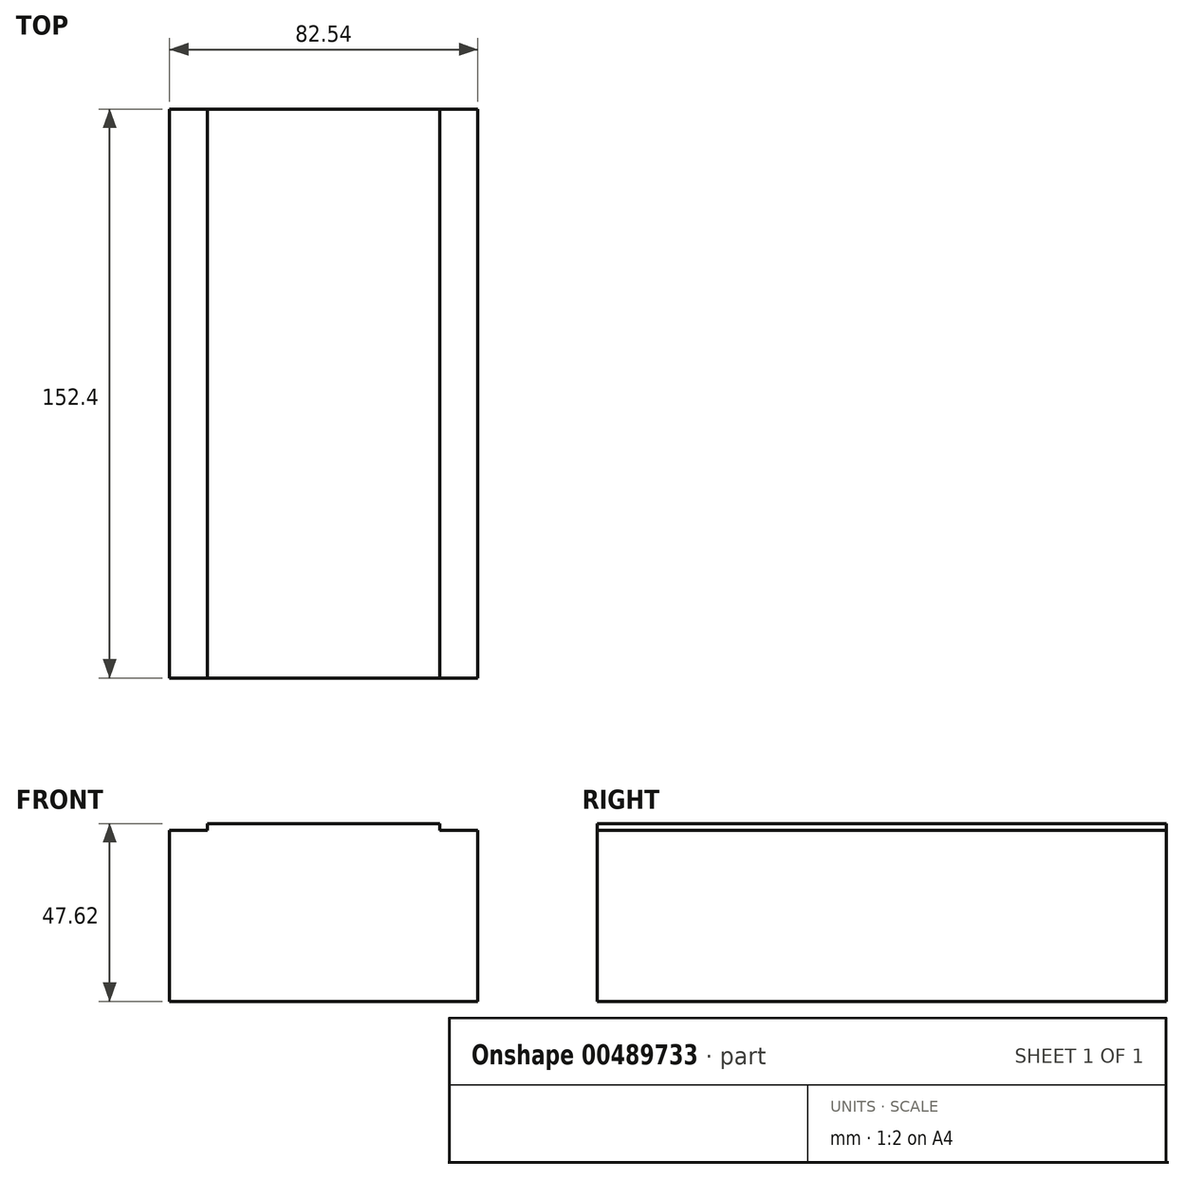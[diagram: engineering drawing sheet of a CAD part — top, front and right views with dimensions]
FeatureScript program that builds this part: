
annotation { "Feature Type Name" : "Feature", "Feature Type Description" : "" }
export const myFeature = defineFeature(function(context is Context, id is Id, definition is map)
    precondition{}
    {
        {
            var Q0;
            Q0=qCreatedBy(makeId("Front.planeOp"),FACE);
            var sketch = newSketch(context, id + "F0", { "sketchPlane" : qUnion([Q0])});
            skLineSegment(sketch, "E0.bottom", {"start": v(31.11, 23.81) * mm, "end": v(-31.11, 23.81) * mm});
            skLineSegment(sketch, "E0.top", {"start": v(41.27, -23.81) * mm, "end": v(-41.28, -23.81) * mm});
            skLineSegment(sketch, "E0.left", {"start": v(41.28, 22.03) * mm, "end": v(41.27, -23.81) * mm});
            skLineSegment(sketch, "E0.right", {"start": v(-41.27, 22.03) * mm, "end": v(-41.28, -23.81) * mm});
            skPoint(sketch, "E0.middle", {"position": v(0, 0) * mm});
            skLineSegment(sketch, "E1.top", {"start": v(-41.27, 22.03) * mm, "end": v(-31.11, 22.03) * mm});
            skLineSegment(sketch, "E1.right", {"start": v(-31.11, 23.81) * mm, "end": v(-31.11, 22.03) * mm});
            skPoint(sketch, "E2.orphan", {"position": v(-41.27, 23.81) * mm});
            skLineSegment(sketch, "E3.MirrorCS", {"start": v(41.27, 22.03) * mm, "end": v(31.11, 22.03) * mm});
            skLineSegment(sketch, "E4.MirrorCS", {"start": v(31.11, 23.81) * mm, "end": v(31.11, 22.03) * mm});
            skPoint(sketch, "E5.orphan", {"position": v(41.28, 23.81) * mm});
            skSolve(sketch);
        }
        {
            var Q0;
            Q0=makeQuery(id+"F0.imprint","IMPRINT",FACE,{"disambiguationData":[TD([[makeQuery(id+"F0.imprint","IMPRINT",EDGE,{"derivedFrom":sQuery(id+"F0.wireOp",EDGE,"E0.bottom")}),1.0]])]});
            extrude(context, id + "F1", {"entities" : qUnion([Q0]), "depth" : 152.4 * mm});
        }
    });
